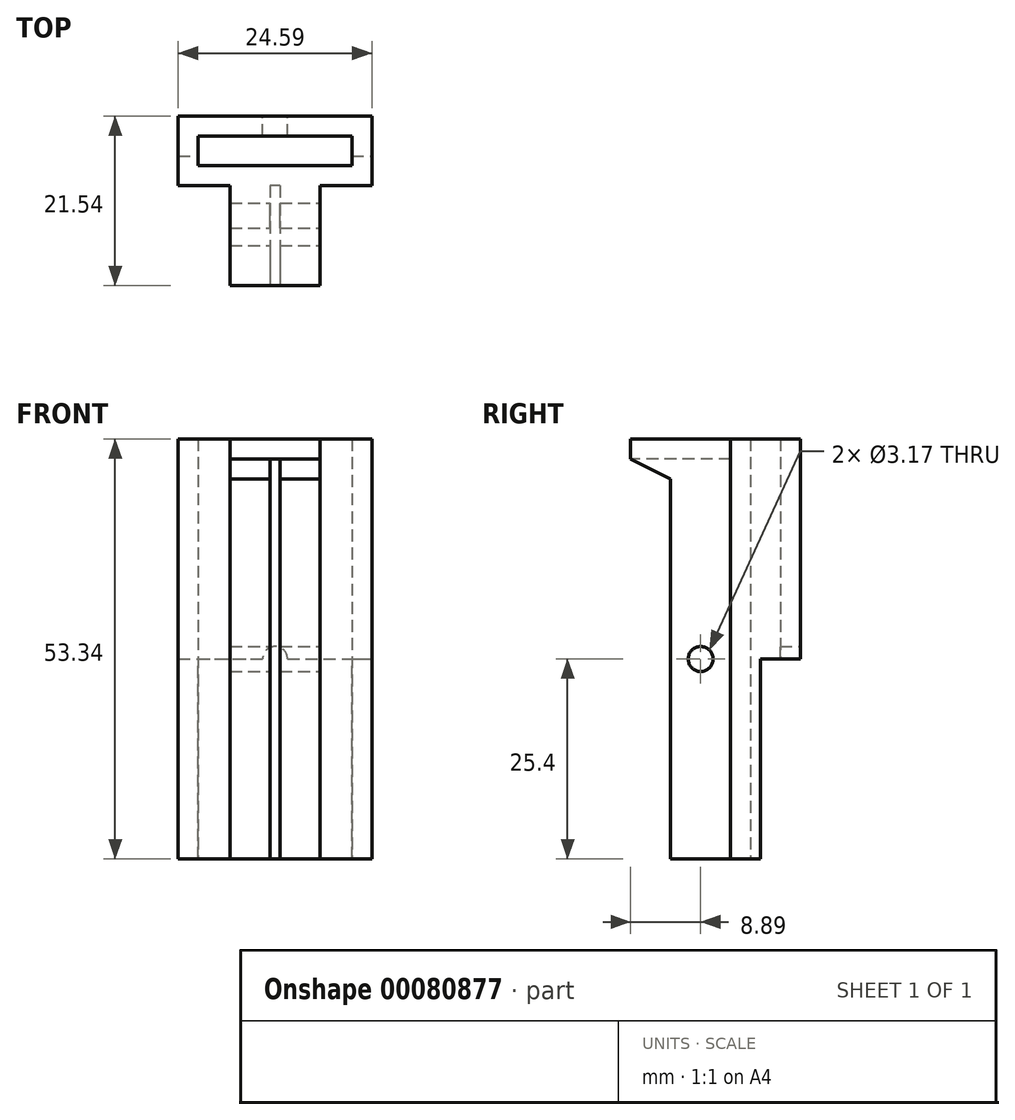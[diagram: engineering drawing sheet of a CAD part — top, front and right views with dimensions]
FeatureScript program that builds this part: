
annotation { "Feature Type Name" : "Feature", "Feature Type Description" : "" }
export const myFeature = defineFeature(function(context is Context, id is Id, definition is map)
    precondition{}
    {
        {
            var Q0;
            Q0=qCreatedBy(makeId("Top.planeOp"),FACE);
            var sketch = newSketch(context, id + "F0", { "sketchPlane" : qUnion([Q0])});
            skLineSegment(sketch, "E0.bottom", {"start": v(0, 0) * mm, "end": v(24.59, 0) * mm});
            skLineSegment(sketch, "E0.top", {"start": v(0, 8.84) * mm, "end": v(5.08, 8.84) * mm});
            skLineSegment(sketch, "E0.left", {"start": v(0, 0) * mm, "end": v(0, 8.84) * mm});
            skLineSegment(sketch, "E0.right", {"start": v(24.59, 0) * mm, "end": v(24.59, 8.84) * mm});
            skLineSegment(sketch, "E1.bottom", {"start": v(6.58, 0) * mm, "end": v(18, 0) * mm});
            skLineSegment(sketch, "E1.top", {"start": v(6.58, -12.7) * mm, "end": v(18, -12.7) * mm});
            skLineSegment(sketch, "E1.left", {"start": v(6.58, 0) * mm, "end": v(6.58, -12.7) * mm});
            skLineSegment(sketch, "E1.right", {"start": v(18, 0) * mm, "end": v(18, -12.7) * mm});
            skLineSegment(sketch, "E2.bottom", {"start": v(2.54, 6.3) * mm, "end": v(5.08, 6.3) * mm});
            skLineSegment(sketch, "E2.top", {"start": v(2.54, 2.54) * mm, "end": v(22.05, 2.54) * mm});
            skLineSegment(sketch, "E2.left", {"start": v(2.54, 6.3) * mm, "end": v(2.54, 2.54) * mm});
            skLineSegment(sketch, "E2.right", {"start": v(22.05, 6.3) * mm, "end": v(22.05, 2.54) * mm});
            skLineSegment(sketch, "E3", {"start": v(12.3, 8.84) * mm, "end": v(12.3, 0) * mm});
            skLineSegment(sketch, "E4.trimOffspring", {"start": v(19.5, 8.84) * mm, "end": v(24.59, 8.84) * mm});
            skLineSegment(sketch, "E5.trimOffspring", {"start": v(19.5, 6.3) * mm, "end": v(22.05, 6.3) * mm});
            skLineSegment(sketch, "E6", {"start": v(5.08, 8.84) * mm, "end": v(19.5, 8.84) * mm});
            skLineSegment(sketch, "E7", {"start": v(5.08, 6.3) * mm, "end": v(19.5, 6.3) * mm});
            skSolve(sketch);
        }
        {
            var Q0;
            Q0=makeQuery(id+"F0.imprint","IMPRINT",FACE,{"disambiguationData":[TD([[makeQuery(id+"F0.imprint","IMPRINT",EDGE,{"derivedFrom":sQuery(id+"F0.wireOp",EDGE,"E1.top")}),1.0]])]});
            var Q1;
            Q1=makeQuery(id+"F0.imprint","IMPRINT",FACE,{"disambiguationData":[TD([[makeQuery(id+"F0.imprint","IMPRINT",EDGE,{"derivedFrom":sQuery(id+"F0.wireOp",EDGE,"E0.top")}),-1.0]])]});
            var Q2;
            {var subQ8=sQuery(id+"F0.wireOp",EDGE,"E0.right");Q2=makeQuery(id+"F0.imprint","IMPRINT",FACE,{"disambiguationData":[TD([[makeQuery(id+"F0.imprint","IMPRINT",EDGE,{"derivedFrom":subQ8}),1.0]])]});}
            extrude(context, id + "F1", {"entities" : qUnion([Q0, Q1, Q2]), "depth" : 53.34 * mm});
        }
        {
            var Q0;
            Q0=makeQuery(id+"F1.opExtrude","SWEPT_FACE",FACE,{"disambiguationData":[OSD([sQuery(id+"F0.wireOp",EDGE,"E1.right")])]});
            var sketch = newSketch(context, id + "F2", { "sketchPlane" : qUnion([Q0])});
            skLineSegment(sketch, "E8", {"start": v(-12.7, 50.8) * mm, "end": v(-7.62, 48.26) * mm});
            skLineSegment(sketch, "E9", {"start": v(-7.62, 48.26) * mm, "end": v(-7.62, 0) * mm});
            skLineSegment(sketch, "E10", {"start": v(-7.62, 0) * mm, "end": v(-12.7, 0) * mm});
            skLineSegment(sketch, "E11", {"start": v(-12.7, 0) * mm, "end": v(-12.7, 50.8) * mm});
            skCircle(sketch, "E12", {"center": v(-3.81, 25.4) * mm, "radius": 1.59 * mm});
            skSolve(sketch);
        }
        {
            var Q0;
            Q0=makeQuery(id+"F2.imprint","IMPRINT",FACE,{"disambiguationData":[TD([[makeQuery(id+"F2.imprint","IMPRINT",EDGE,{"derivedFrom":sQuery(id+"F2.wireOp",EDGE,"E8")}),-1.0]])]});
            var Q1;
            Q1=makeQuery(id+"F2.imprint","IMPRINT",FACE,{"disambiguationData":[TD([[makeQuery(id+"F2.imprint","IMPRINT",EDGE,{"derivedFrom":sQuery(id+"F2.wireOp",EDGE,"E12")}),1.0]])]});
            extrude(context, id + "F3", {"entities" : qUnion([Q0, Q1]), "operationType" : NewBodyOperationType.REMOVE, "oppositeDirection" : true, "depth" : 25.4 * mm});
        }
        {
            var Q0;
            Q0=makeQuery(id+"F1.opExtrude","CAP_FACE",FACE,{"disambiguationData":[OSD([sQuery(id+"F0.wireOp",EDGE,"E0.bottom"),sQuery(id+"F0.wireOp",EDGE,"E0.top"),sQuery(id+"F0.wireOp",EDGE,"E0.left"),sQuery(id+"F0.wireOp",EDGE,"E0.right"),sQuery(id+"F0.wireOp",EDGE,"E1.top"),sQuery(id+"F0.wireOp",EDGE,"E1.left"),sQuery(id+"F0.wireOp",EDGE,"E1.right"),sQuery(id+"F0.wireOp",EDGE,"E2.bottom"),sQuery(id+"F0.wireOp",EDGE,"E2.top"),sQuery(id+"F0.wireOp",EDGE,"E2.left"),sQuery(id+"F0.wireOp",EDGE,"E2.right"),sQuery(id+"F0.wireOp",EDGE,"5R74wSaL-k5B7-YVsY-JrId-ekZyqKfwHjvl"),sQuery(id+"F0.wireOp",EDGE,"864dc3d5-bcae-4925-92a8-966a68b91c600.MirrorCS"),sQuery(id+"F0.wireOp",EDGE,"E4.trimOffspring"),sQuery(id+"F0.wireOp",EDGE,"E5.trimOffspring")])],"isStart":true});
            var sketch = newSketch(context, id + "F4", { "sketchPlane" : qUnion([Q0])});
            skLineSegment(sketch, "E13.bottom", {"start": v(12.93, 0) * mm, "end": v(11.66, 0) * mm});
            skLineSegment(sketch, "E13.top", {"start": v(12.93, 12.7) * mm, "end": v(11.66, 12.7) * mm});
            skLineSegment(sketch, "E13.left", {"start": v(12.93, 0) * mm, "end": v(12.93, 12.7) * mm});
            skLineSegment(sketch, "E13.right", {"start": v(11.66, 0) * mm, "end": v(11.66, 12.7) * mm});
            skSolve(sketch);
        }
        {
            var Q0;
            {var subQ0=sQuery(id+"F4.wireOp",EDGE,"E13.top");Q0=makeQuery(id+"F4.imprint","IMPRINT",FACE,{"disambiguationData":[TD([[makeQuery(id+"F4.imprint","IMPRINT",EDGE,{"derivedFrom":subQ0}),1.0]])]});}
            var Q1;
            {var subQ0=sQuery(id+"F4.wireOp",EDGE,"E13.bottom");Q1=makeQuery(id+"F4.imprint","IMPRINT",FACE,{"disambiguationData":[TD([[makeQuery(id+"F4.imprint","IMPRINT",EDGE,{"derivedFrom":subQ0}),-1.0]])]});}
            extrude(context, id + "F5", {"entities" : qUnion([Q0, Q1]), "operationType" : NewBodyOperationType.REMOVE, "oppositeDirection" : true, "depth" : 50.8 * mm});
        }
        {
            var Q0;
            Q0=makeQuery(id+"F1.opExtrude","SWEPT_FACE",FACE,{"disambiguationData":[OSD([sQuery(id+"F0.wireOp",EDGE,"E0.top"),sQuery(id+"F0.wireOp",EDGE,"E4.trimOffspring"),sQuery(id+"F0.wireOp",EDGE,"E6")])]});
            var sketch = newSketch(context, id + "F6", { "sketchPlane" : qUnion([Q0])});
            skLineSegment(sketch, "E14", {"start": v(-12.3, 53.34) * mm, "end": v(-12.3, 0) * mm});
            skLineSegment(sketch, "E15", {"start": v(0, 25.4) * mm, "end": v(-24.59, 25.4) * mm});
            skCircle(sketch, "E16", {"center": v(-12.3, 25.4) * mm, "radius": 1.59 * mm});
            skSolve(sketch);
        }
        {
            var Q0;
            {var subQ0=sQuery(id+"F6.wireOp",EDGE,"G6hWRhac-GfrT-Pkvr-KCjT-gaLeKmKOAa4n");var subQ1=sQuery(id+"F6.wireOp",EDGE,"E14");var subQ2=makeQuery(id+"F6.imprint","INTERSECT",VERTEX,{"derivedFrom":[subQ1,subQ0]});Q0=makeQuery(id+"F6.imprint","IMPRINT",FACE,{"disambiguationData":[TD([[makeQuery(id+"F6.imprint","IMPRINT",EDGE,{"disambiguationData":[TD([[subQ2,-1.0]])],"derivedFrom":subQ1}),1.0]])]});}
            var Q1;
            {var subQ0=sQuery(id+"F6.wireOp",EDGE,"6sSWnMn8-VdU5-gXYE-3gaH-251aTxTLA8IV");var subQ1=sQuery(id+"F6.wireOp",EDGE,"E14");var subQ2=makeQuery(id+"F6.imprint","INTERSECT",VERTEX,{"disambiguationData":[OD(0.0)],"derivedFrom":[subQ1,subQ0]});Q1=makeQuery(id+"F6.imprint","IMPRINT",FACE,{"disambiguationData":[TD([[makeQuery(id+"F6.imprint","IMPRINT",EDGE,{"disambiguationData":[TD([[subQ2,-1.0]])],"derivedFrom":subQ1}),1.0]])]});}
            var Q2;
            {var subQ0=sQuery(id+"F6.wireOp",EDGE,"6sSWnMn8-VdU5-gXYE-3gaH-251aTxTLA8IV");var subQ1=sQuery(id+"F6.wireOp",EDGE,"E14");var subQ2=makeQuery(id+"F6.imprint","INTERSECT",VERTEX,{"disambiguationData":[OD(0.0)],"derivedFrom":[subQ1,subQ0]});Q2=makeQuery(id+"F6.imprint","IMPRINT",FACE,{"disambiguationData":[TD([[makeQuery(id+"F6.imprint","IMPRINT",EDGE,{"disambiguationData":[TD([[subQ2,-1.0]])],"derivedFrom":subQ1}),-1.0]])]});}
            var Q3;
            {var subQ0=sQuery(id+"F6.wireOp",EDGE,"G6hWRhac-GfrT-Pkvr-KCjT-gaLeKmKOAa4n");var subQ1=sQuery(id+"F6.wireOp",EDGE,"E14");var subQ2=makeQuery(id+"F6.imprint","INTERSECT",VERTEX,{"derivedFrom":[subQ1,subQ0]});Q3=makeQuery(id+"F6.imprint","IMPRINT",FACE,{"disambiguationData":[TD([[makeQuery(id+"F6.imprint","IMPRINT",EDGE,{"disambiguationData":[TD([[subQ2,-1.0]])],"derivedFrom":subQ1}),-1.0]])]});}
            extrude(context, id + "F7", {"entities" : qUnion([Q0, Q1, Q2, Q3]), "operationType" : NewBodyOperationType.REMOVE, "oppositeDirection" : true, "depth" : 5.08 * mm});
        }
    });
